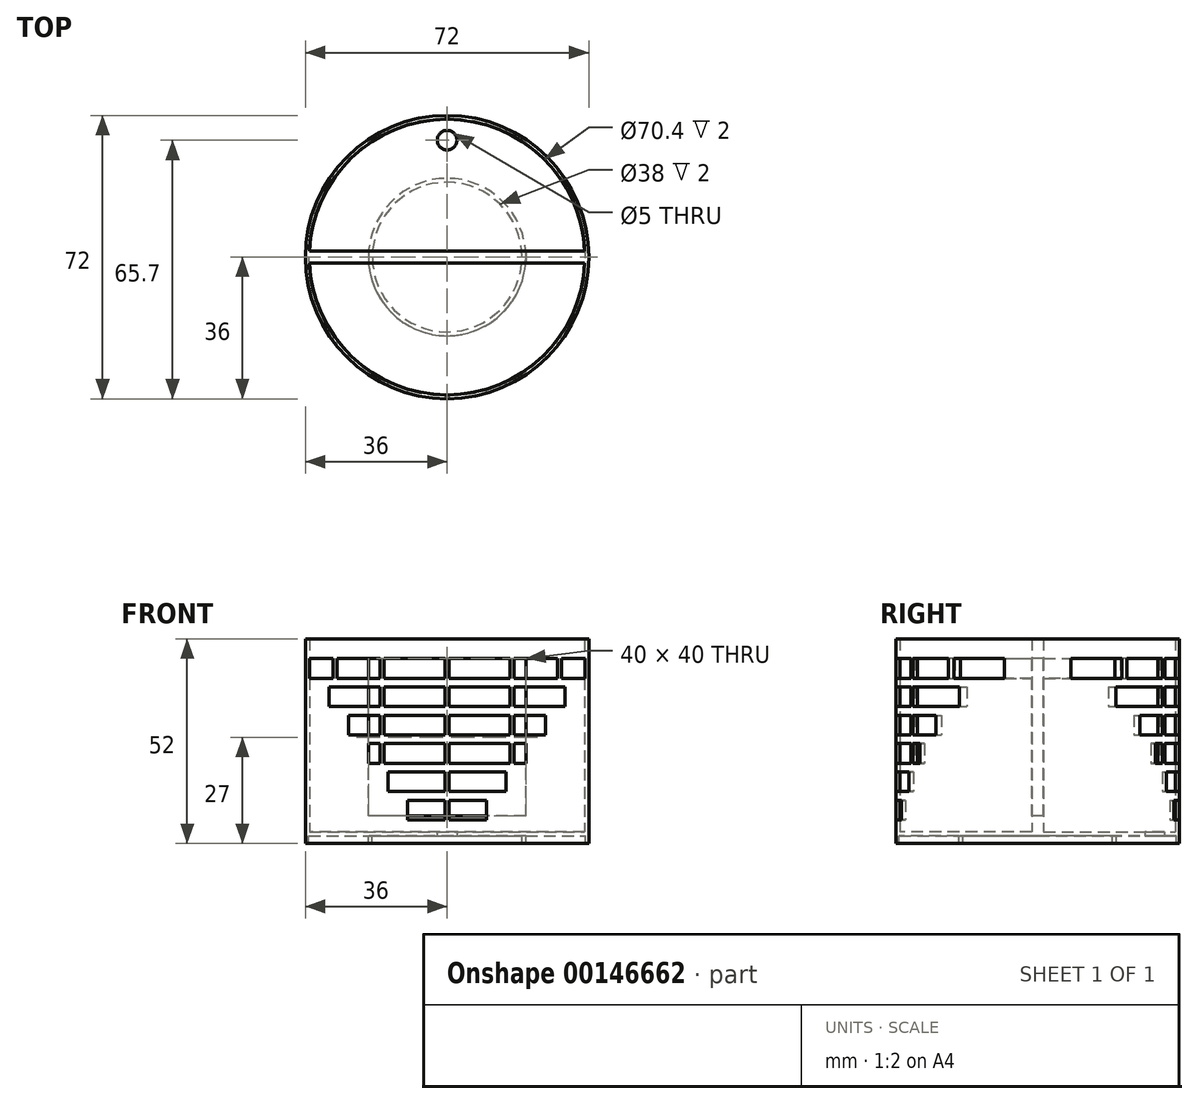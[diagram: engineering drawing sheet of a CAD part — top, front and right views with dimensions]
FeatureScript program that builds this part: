
annotation { "Feature Type Name" : "Feature", "Feature Type Description" : "" }
export const myFeature = defineFeature(function(context is Context, id is Id, definition is map)
    precondition{}
    {
        {
            var Q0;
            Q0=qCreatedBy(makeId("Top.planeOp"),FACE);
            var sketch = newSketch(context, id + "F0", { "sketchPlane" : qUnion([Q0])});
            skCircle(sketch, "E0", {"center": v(0, 0) * mm, "radius": 36 * mm});
            skCircle(sketch, "E1", {"center": v(0, 0) * mm, "radius": 35 * mm});
            skSolve(sketch);
        }
        {
            var Q0;
            Q0=qSketchRegion(id+"F0",true);
            extrude(context, id + "F1", {"entities" : qUnion([Q0]), "depth" : 50 * mm});
        }
        {
            var Q0;
            Q0=qCreatedBy(makeId("Front.planeOp"),FACE);
            var sketch = newSketch(context, id + "F2", { "sketchPlane" : qUnion([Q0])});
            skLineSegment(sketch, "E2", {"start": v(0, 90.5) * mm, "end": v(0, 29.68) * mm, "construction": true});
            skLineSegment(sketch, "E3.bottom", {"start": v(35, 40) * mm, "end": v(-35, 40) * mm});
            skLineSegment(sketch, "E3.top", {"start": v(35, 45) * mm, "end": v(-35, 45) * mm});
            skLineSegment(sketch, "E3.left", {"start": v(35, 40) * mm, "end": v(35, 45) * mm});
            skLineSegment(sketch, "E3.right", {"start": v(-35, 40) * mm, "end": v(-35, 45) * mm});
            skPoint(sketch, "E3.middle", {"position": v(0, 42.5) * mm});
            skLineSegment(sketch, "E4.bottom", {"start": v(30, 32.8) * mm, "end": v(-30, 32.8) * mm});
            skLineSegment(sketch, "E4.top", {"start": v(30, 37.8) * mm, "end": v(-30, 37.8) * mm});
            skLineSegment(sketch, "E4.left", {"start": v(30, 32.8) * mm, "end": v(30, 37.8) * mm});
            skLineSegment(sketch, "E4.right", {"start": v(-30, 32.8) * mm, "end": v(-30, 37.8) * mm});
            skPoint(sketch, "E4.middle", {"position": v(0, 35.3) * mm});
            skLineSegment(sketch, "E5.bottom", {"start": v(25, 25.6) * mm, "end": v(-25, 25.6) * mm});
            skLineSegment(sketch, "E5.top", {"start": v(25, 30.6) * mm, "end": v(-25, 30.6) * mm});
            skLineSegment(sketch, "E5.left", {"start": v(25, 25.6) * mm, "end": v(25, 30.6) * mm});
            skLineSegment(sketch, "E5.right", {"start": v(-25, 25.6) * mm, "end": v(-25, 30.6) * mm});
            skPoint(sketch, "E5.middle", {"position": v(0, 28.1) * mm});
            skLineSegment(sketch, "E6.bottom", {"start": v(20, 18.4) * mm, "end": v(-20, 18.4) * mm});
            skLineSegment(sketch, "E6.top", {"start": v(20, 23.4) * mm, "end": v(-20, 23.4) * mm});
            skLineSegment(sketch, "E6.left", {"start": v(20, 18.4) * mm, "end": v(20, 23.4) * mm});
            skLineSegment(sketch, "E6.right", {"start": v(-20, 18.4) * mm, "end": v(-20, 23.4) * mm});
            skPoint(sketch, "E6.middle", {"position": v(0, 20.9) * mm});
            skLineSegment(sketch, "E7.bottom", {"start": v(15, 11.2) * mm, "end": v(-15, 11.2) * mm});
            skLineSegment(sketch, "E7.top", {"start": v(15, 16.2) * mm, "end": v(-15, 16.2) * mm});
            skLineSegment(sketch, "E7.left", {"start": v(15, 11.2) * mm, "end": v(15, 16.2) * mm});
            skLineSegment(sketch, "E7.right", {"start": v(-15, 11.2) * mm, "end": v(-15, 16.2) * mm});
            skPoint(sketch, "E7.middle", {"position": v(0, 13.7) * mm});
            skLineSegment(sketch, "E8.bottom", {"start": v(10, 4) * mm, "end": v(-10, 4) * mm});
            skLineSegment(sketch, "E8.top", {"start": v(10, 9) * mm, "end": v(-10, 9) * mm});
            skLineSegment(sketch, "E8.left", {"start": v(10, 4) * mm, "end": v(10, 9) * mm});
            skLineSegment(sketch, "E8.right", {"start": v(-10, 4) * mm, "end": v(-10, 9) * mm});
            skPoint(sketch, "E8.middle", {"position": v(0, 6.5) * mm});
            skSolve(sketch);
        }
        {
            var Q0;
            Q0 = qSketchRegion(id + "F2", true);
            extrude(context, id + "F3", {"entities" : qUnion([Q0]), "operationType" : NewBodyOperationType.REMOVE, "depth" : 39 * mm, "hasSecondDirection" : true, "secondDirectionOppositeDirection" : true, "secondDirectionDepth" : 39 * mm});
        }
        {
            var Q0;
            Q0=qCreatedBy(makeId("Front.planeOp"),FACE);
            var sketch = newSketch(context, id + "F4", { "sketchPlane" : qUnion([Q0])});
            skLineSegment(sketch, "E9.bottom", {"start": v(-0.5, 50) * mm, "end": v(0.5, 50) * mm});
            skLineSegment(sketch, "E9.top", {"start": v(-0.5, 0) * mm, "end": v(0.5, 0) * mm});
            skLineSegment(sketch, "E9.left", {"start": v(-0.5, 50) * mm, "end": v(-0.5, 0) * mm});
            skLineSegment(sketch, "E9.right", {"start": v(0.5, 50) * mm, "end": v(0.5, 0) * mm});
            skLineSegment(sketch, "E10.bottom", {"start": v(-17, 50) * mm, "end": v(-16, 50) * mm});
            skLineSegment(sketch, "E10.top", {"start": v(-17, 0) * mm, "end": v(-16, 0) * mm});
            skLineSegment(sketch, "E10.left", {"start": v(-17, 50) * mm, "end": v(-17, 0) * mm});
            skLineSegment(sketch, "E10.right", {"start": v(-16, 50) * mm, "end": v(-16, 0) * mm});
            skLineSegment(sketch, "E11.bottom", {"start": v(16, 50) * mm, "end": v(17, 50) * mm});
            skLineSegment(sketch, "E11.top", {"start": v(16, 0) * mm, "end": v(17, 0) * mm});
            skLineSegment(sketch, "E11.left", {"start": v(16, 50) * mm, "end": v(16, 0) * mm});
            skLineSegment(sketch, "E11.right", {"start": v(17, 50) * mm, "end": v(17, 0) * mm});
            skLineSegment(sketch, "E12", {"start": v(0, 56.03) * mm, "end": v(0, 88.6) * mm, "construction": true});
            skLineSegment(sketch, "E13.bottom", {"start": v(-29, 50) * mm, "end": v(-28, 50) * mm});
            skLineSegment(sketch, "E13.top", {"start": v(-29, 40) * mm, "end": v(-28, 40) * mm});
            skLineSegment(sketch, "E13.left", {"start": v(-29, 50) * mm, "end": v(-29, 40) * mm});
            skLineSegment(sketch, "E13.right", {"start": v(-28, 50) * mm, "end": v(-28, 40) * mm});
            skLineSegment(sketch, "E14.bottom", {"start": v(28, 50) * mm, "end": v(29, 50) * mm});
            skLineSegment(sketch, "E14.top", {"start": v(28, 40) * mm, "end": v(29, 40) * mm});
            skLineSegment(sketch, "E14.left", {"start": v(28, 50) * mm, "end": v(28, 40) * mm});
            skLineSegment(sketch, "E14.right", {"start": v(29, 50) * mm, "end": v(29, 40) * mm});
            skSolve(sketch);
        }
        {
            var Q0;
            Q0=qSketchRegion(id+"F4",true);
            var Q1;
            Q1=makeQuery(id+"F1.opExtrude","SWEPT_FACE",FACE,{"disambiguationData":[OSD([sQuery(id+"F0.wireOp",EDGE,"E0")])]});
            var Q2;
            Q2=makeQuery(id+"F1.opExtrude","SWEPT_FACE",FACE,{"disambiguationData":[OSD([sQuery(id+"F0.wireOp",EDGE,"E0")])]});
            extrude(context, id + "F5", {"entities" : qUnion([Q0]), "operationType" : NewBodyOperationType.ADD, "endBound" : BoundingType.UP_TO_SURFACE, "endBoundEntityFace" : qUnion([Q1]), "depth" : 25 * mm, "hasSecondDirection" : true, "secondDirectionBound" : SecondDirectionBoundingType.UP_TO_SURFACE, "secondDirectionOppositeDirection" : true, "secondDirectionBoundEntityFace" : qUnion([Q2]), "secondDirectionDepth" : 25 * mm});
        }
        {
            var Q0;
            Q0=qCreatedBy(makeId("Top.planeOp"),FACE);
            var sketch = newSketch(context, id + "F6", { "sketchPlane" : qUnion([Q0])});
            skCircle(sketch, "E15", {"center": v(0, 0) * mm, "radius": 35 * mm});
            skSolve(sketch);
        }
        {
            var Q0;
            Q0=qSketchRegion(id+"F6",true);
            var Q1;
            Q1=makeQuery(id+"F1.opExtrude","CAP_FACE",FACE,{"disambiguationData":[OSD([sQuery(id+"F0.wireOp",EDGE,"E0"),sQuery(id+"F0.wireOp",EDGE,"E1")])],"isStart":false});
            extrude(context, id + "F7", {"entities" : qUnion([Q0]), "operationType" : NewBodyOperationType.REMOVE, "endBound" : BoundingType.THROUGH_ALL, "endBoundEntityFace" : qUnion([Q1]), "depth" : 25 * mm});
        }
        {
            var Q0;
            Q0=qCreatedBy(makeId("Top.planeOp"),FACE);
            var sketch = newSketch(context, id + "F8", { "sketchPlane" : qUnion([Q0])});
            skLineSegment(sketch, "E16.bottom", {"start": v(-35.53, 1.5) * mm, "end": v(35.48, 1.5) * mm});
            skLineSegment(sketch, "E16.top", {"start": v(-35.53, -1.5) * mm, "end": v(35.48, -1.5) * mm});
            skLineSegment(sketch, "E16.left", {"start": v(-35.53, 1.5) * mm, "end": v(-35.53, -1.5) * mm});
            skLineSegment(sketch, "E16.right", {"start": v(35.48, 1.5) * mm, "end": v(35.48, -1.5) * mm});
            skSolve(sketch);
        }
        {
            var Q0;
            Q0 = qSketchRegion(id + "F8", true);
            var Q1;
            Q1=makeQuery(id+"F5.boolean.opBoolean","MERGE",FACE,{"derivedFrom":[makeQuery(id+"F1.opExtrude","CAP_FACE",FACE,{"disambiguationData":[OSD([sQuery(id+"F0.wireOp",EDGE,"E0"),sQuery(id+"F0.wireOp",EDGE,"E1")])],"isStart":false}),makeQuery(id+"F5.opExtrude","SWEPT_FACE",FACE,{"disambiguationData":[OSD([sQuery(id+"F4.wireOp",EDGE,"E9.bottom")])]}),makeQuery(id+"F5.opExtrude","SWEPT_FACE",FACE,{"disambiguationData":[OSD([sQuery(id+"F4.wireOp",EDGE,"E10.bottom")])]}),makeQuery(id+"F5.opExtrude","SWEPT_FACE",FACE,{"disambiguationData":[OSD([sQuery(id+"F4.wireOp",EDGE,"E11.bottom")])]})]});
            extrude(context, id + "F9", {"entities" : qUnion([Q0]), "operationType" : NewBodyOperationType.ADD, "endBound" : BoundingType.UP_TO_SURFACE, "endBoundEntityFace" : qUnion([Q1]), "depth" : 25 * mm});
        }
        {
            var Q0;
            Q0=makeQuery(id+"F9.opExtrude","SWEPT_FACE",FACE,{"disambiguationData":[OSD([sQuery(id+"F8.wireOp",EDGE,"E16.top")])]});
            var sketch = newSketch(context, id + "F10", { "sketchPlane" : qUnion([Q0])});
            skLineSegment(sketch, "E17.bottom", {"start": v(-20, 45) * mm, "end": v(20, 45) * mm});
            skLineSegment(sketch, "E17.top", {"start": v(-20, 5) * mm, "end": v(20, 5) * mm});
            skLineSegment(sketch, "E17.left", {"start": v(-20, 45) * mm, "end": v(-20, 5) * mm});
            skLineSegment(sketch, "E17.right", {"start": v(20, 45) * mm, "end": v(20, 5) * mm});
            skLineSegment(sketch, "E18", {"start": v(0, 45) * mm, "end": v(0, 5) * mm, "construction": true});
            skSolve(sketch);
        }
        {
            var Q0;
            Q0 = qSketchRegion(id + "F10", true);
            extrude(context, id + "F11", {"entities" : qUnion([Q0]), "operationType" : NewBodyOperationType.REMOVE, "endBound" : BoundingType.SYMMETRIC, "oppositeDirection" : true, "depth" : 9.8 * mm});
        }
        {
            var Q0;
            Q0=makeQuery(id+"F9.boolean.opBoolean","MERGE",FACE,{"derivedFrom":[makeQuery(id+"F5.boolean.opBoolean","MERGE",FACE,{"derivedFrom":[makeQuery(id+"F1.opExtrude","CAP_FACE",FACE,{"disambiguationData":[OSD([sQuery(id+"F0.wireOp",EDGE,"E0"),sQuery(id+"F0.wireOp",EDGE,"E1")])],"isStart":true}),makeQuery(id+"F5.opExtrude","SWEPT_FACE",FACE,{"disambiguationData":[OSD([sQuery(id+"F4.wireOp",EDGE,"E9.top")])]}),makeQuery(id+"F5.opExtrude","SWEPT_FACE",FACE,{"disambiguationData":[OSD([sQuery(id+"F4.wireOp",EDGE,"E10.top")])]}),makeQuery(id+"F5.opExtrude","SWEPT_FACE",FACE,{"disambiguationData":[OSD([sQuery(id+"F4.wireOp",EDGE,"E11.top")])]})]}),makeQuery(id+"F9.opExtrude","CAP_FACE",FACE,{"disambiguationData":[OSD([sQuery(id+"F8.wireOp",EDGE,"E16.bottom"),sQuery(id+"F8.wireOp",EDGE,"E16.top"),sQuery(id+"F8.wireOp",EDGE,"E16.left"),sQuery(id+"F8.wireOp",EDGE,"E16.right")])],"isStart":true})]});
            var sketch = newSketch(context, id + "F12", { "sketchPlane" : qUnion([Q0])});
            skCircle(sketch, "E19", {"center": v(0, 0) * mm, "radius": 35 * mm});
            skSolve(sketch);
        }
        {
            var Q0;
            Q0 = qSketchRegion(id + "F12", true);
            extrude(context, id + "F13", {"entities" : qUnion([Q0]), "operationType" : NewBodyOperationType.ADD, "oppositeDirection" : true, "depth" : 1 * mm});
        }
        {
            var Q0;
            Q0=makeQuery(id+"F13.boolean.opBoolean","MERGE",FACE,{"derivedFrom":[makeQuery(id+"F9.boolean.opBoolean","MERGE",FACE,{"derivedFrom":[makeQuery(id+"F5.boolean.opBoolean","MERGE",FACE,{"derivedFrom":[makeQuery(id+"F1.opExtrude","CAP_FACE",FACE,{"disambiguationData":[OSD([sQuery(id+"F0.wireOp",EDGE,"E0"),sQuery(id+"F0.wireOp",EDGE,"E1")])],"isStart":true}),makeQuery(id+"F5.opExtrude","SWEPT_FACE",FACE,{"disambiguationData":[OSD([sQuery(id+"F4.wireOp",EDGE,"E9.top")])]}),makeQuery(id+"F5.opExtrude","SWEPT_FACE",FACE,{"disambiguationData":[OSD([sQuery(id+"F4.wireOp",EDGE,"E10.top")])]}),makeQuery(id+"F5.opExtrude","SWEPT_FACE",FACE,{"disambiguationData":[OSD([sQuery(id+"F4.wireOp",EDGE,"E11.top")])]})]}),makeQuery(id+"F9.opExtrude","CAP_FACE",FACE,{"disambiguationData":[OSD([sQuery(id+"F8.wireOp",EDGE,"E16.bottom"),sQuery(id+"F8.wireOp",EDGE,"E16.top"),sQuery(id+"F8.wireOp",EDGE,"E16.left"),sQuery(id+"F8.wireOp",EDGE,"E16.right")])],"isStart":true})]}),makeQuery(id+"F13.opExtrude","CAP_FACE",FACE,{"disambiguationData":[OSD([sQuery(id+"F12.wireOp",EDGE,"E19")])],"isStart":true})]});
            var sketch = newSketch(context, id + "F14", { "sketchPlane" : qUnion([Q0])});
            skCircle(sketch, "E20", {"center": v(0, 0) * mm, "radius": 36 * mm});
            skCircle(sketch, "E21", {"center": v(0, 0) * mm, "radius": 35.2 * mm});
            skSolve(sketch);
        }
        {
            var Q0;
            Q0 = qSketchRegion(id + "F14", true);
            extrude(context, id + "F15", {"entities" : qUnion([Q0]), "operationType" : NewBodyOperationType.ADD, "depth" : 2 * mm});
        }
        {
            var Q0;
            Q0=makeQuery(id+"F13.boolean.opBoolean","MERGE",FACE,{"derivedFrom":[makeQuery(id+"F9.boolean.opBoolean","MERGE",FACE,{"derivedFrom":[makeQuery(id+"F5.boolean.opBoolean","MERGE",FACE,{"derivedFrom":[makeQuery(id+"F1.opExtrude","CAP_FACE",FACE,{"disambiguationData":[OSD([sQuery(id+"F0.wireOp",EDGE,"E0"),sQuery(id+"F0.wireOp",EDGE,"E1")])],"isStart":true}),makeQuery(id+"F5.opExtrude","SWEPT_FACE",FACE,{"disambiguationData":[OSD([sQuery(id+"F4.wireOp",EDGE,"E9.top")])]}),makeQuery(id+"F5.opExtrude","SWEPT_FACE",FACE,{"disambiguationData":[OSD([sQuery(id+"F4.wireOp",EDGE,"E10.top")])]}),makeQuery(id+"F5.opExtrude","SWEPT_FACE",FACE,{"disambiguationData":[OSD([sQuery(id+"F4.wireOp",EDGE,"E11.top")])]})]}),makeQuery(id+"F9.opExtrude","CAP_FACE",FACE,{"disambiguationData":[OSD([sQuery(id+"F8.wireOp",EDGE,"E16.bottom"),sQuery(id+"F8.wireOp",EDGE,"E16.top"),sQuery(id+"F8.wireOp",EDGE,"E16.left"),sQuery(id+"F8.wireOp",EDGE,"E16.right")])],"isStart":true})]}),makeQuery(id+"F13.opExtrude","CAP_FACE",FACE,{"disambiguationData":[OSD([sQuery(id+"F12.wireOp",EDGE,"E19")])],"isStart":true})]});
            var sketch = newSketch(context, id + "F16", { "sketchPlane" : qUnion([Q0])});
            skCircle(sketch, "E22", {"center": v(0, 0) * mm, "radius": 20 * mm});
            skCircle(sketch, "E23", {"center": v(0, 0) * mm, "radius": 19 * mm});
            skSolve(sketch);
        }
        {
            var Q0;
            Q0 = qSketchRegion(id + "F16", true);
            var Q1;
            Q1=makeQuery(id+"F15.opExtrude","CAP_FACE",FACE,{"disambiguationData":[OSD([sQuery(id+"F14.wireOp",EDGE,"E20"),sQuery(id+"F14.wireOp",EDGE,"E21")])],"isStart":false});
            extrude(context, id + "F17", {"entities" : qUnion([Q0]), "operationType" : NewBodyOperationType.ADD, "endBound" : BoundingType.UP_TO_SURFACE, "endBoundEntityFace" : qUnion([Q1]), "depth" : 25 * mm});
        }
        {
            var Q0;
            Q0=makeQuery(id+"F17.boolean.opBoolean","SPLIT",FACE,{"disambiguationData":[TD([makeQuery(id+"F17.opExtrude","SWEPT_FACE",FACE,{"disambiguationData":[OSD([sQuery(id+"F16.wireOp",EDGE,"E23")])]})])],"derivedFrom":makeQuery(id+"F13.boolean.opBoolean","MERGE",FACE,{"derivedFrom":[makeQuery(id+"F9.boolean.opBoolean","MERGE",FACE,{"derivedFrom":[makeQuery(id+"F5.boolean.opBoolean","MERGE",FACE,{"derivedFrom":[makeQuery(id+"F1.opExtrude","CAP_FACE",FACE,{"disambiguationData":[OSD([sQuery(id+"F0.wireOp",EDGE,"E0"),sQuery(id+"F0.wireOp",EDGE,"E1")])],"isStart":true}),makeQuery(id+"F5.opExtrude","SWEPT_FACE",FACE,{"disambiguationData":[OSD([sQuery(id+"F4.wireOp",EDGE,"E9.top")])]}),makeQuery(id+"F5.opExtrude","SWEPT_FACE",FACE,{"disambiguationData":[OSD([sQuery(id+"F4.wireOp",EDGE,"E10.top")])]}),makeQuery(id+"F5.opExtrude","SWEPT_FACE",FACE,{"disambiguationData":[OSD([sQuery(id+"F4.wireOp",EDGE,"E11.top")])]})]}),makeQuery(id+"F9.opExtrude","CAP_FACE",FACE,{"disambiguationData":[OSD([sQuery(id+"F8.wireOp",EDGE,"E16.bottom"),sQuery(id+"F8.wireOp",EDGE,"E16.top"),sQuery(id+"F8.wireOp",EDGE,"E16.left"),sQuery(id+"F8.wireOp",EDGE,"E16.right")])],"isStart":true})]}),makeQuery(id+"F13.opExtrude","CAP_FACE",FACE,{"disambiguationData":[OSD([sQuery(id+"F12.wireOp",EDGE,"E19")])],"isStart":true})]})});
            var sketch = newSketch(context, id + "F18", { "sketchPlane" : qUnion([Q0])});
            skCircle(sketch, "E24", {"center": v(0, -29.7) * mm, "radius": 2.5 * mm});
            skSolve(sketch);
        }
        {
            var Q0;
            Q0 = qSketchRegion(id + "F18", true);
            extrude(context, id + "F19", {"entities" : qUnion([Q0]), "operationType" : NewBodyOperationType.REMOVE, "oppositeDirection" : true, "depth" : 3 * mm});
        }
    });
